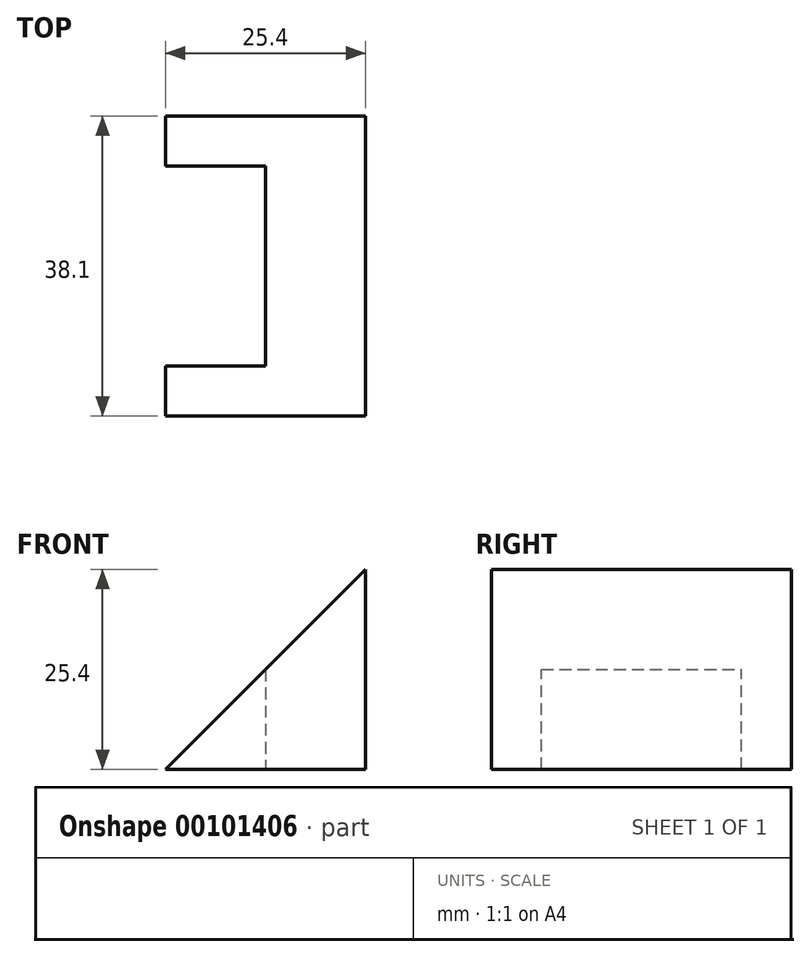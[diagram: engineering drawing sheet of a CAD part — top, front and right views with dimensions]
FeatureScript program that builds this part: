
annotation { "Feature Type Name" : "Feature", "Feature Type Description" : "" }
export const myFeature = defineFeature(function(context is Context, id is Id, definition is map)
    precondition{}
    {
        {
            var Q0;
            Q0=qCreatedBy(makeId("Front.planeOp"),FACE);
            var sketch = newSketch(context, id + "F0", { "sketchPlane" : qUnion([Q0])});
            skLineSegment(sketch, "E0", {"start": v(0, 0) * mm, "end": v(-25.4, 0) * mm});
            skLineSegment(sketch, "E1", {"start": v(-25.4, 0) * mm, "end": v(0, 25.4) * mm});
            skLineSegment(sketch, "E2", {"start": v(0, 25.4) * mm, "end": v(0, 0) * mm});
            skSolve(sketch);
        }
        {
            var Q0;
            Q0 = qSketchRegion(id + "F0", true);
            extrude(context, id + "F1", {"entities" : qUnion([Q0]), "endBound" : BoundingType.SYMMETRIC, "depth" : 38.1 * mm});
        }
        {
            var Q0;
            Q0=qCreatedBy(makeId("Front.planeOp"),FACE);
            var sketch = newSketch(context, id + "F2", { "sketchPlane" : qUnion([Q0])});
            skLineSegment(sketch, "E3", {"start": v(-12.7, 12.7) * mm, "end": v(-12.7, 0) * mm});
            skLineSegment(sketch, "E4", {"start": v(-12.7, 0) * mm, "end": v(-25.4, 0) * mm});
            skLineSegment(sketch, "E5", {"start": v(-25.4, 0) * mm, "end": v(-12.7, 12.7) * mm});
            skSolve(sketch);
        }
        {
            var Q0;
            Q0 = qSketchRegion(id + "F2", true);
            extrude(context, id + "F3", {"entities" : qUnion([Q0]), "operationType" : NewBodyOperationType.REMOVE, "endBound" : BoundingType.SYMMETRIC, "depth" : 25.4 * mm});
        }
    });
